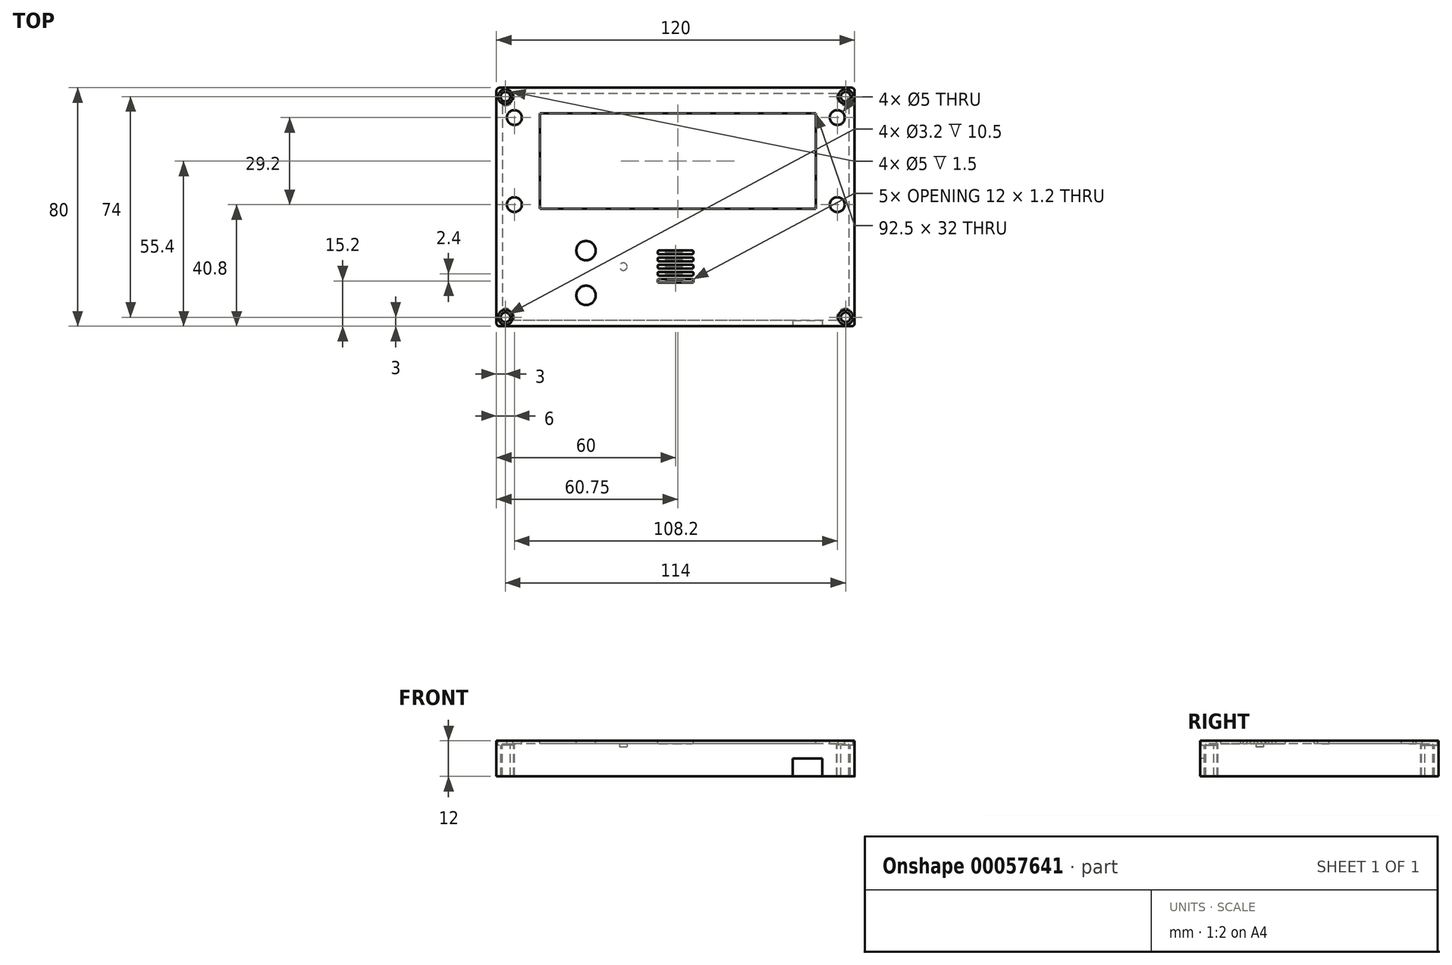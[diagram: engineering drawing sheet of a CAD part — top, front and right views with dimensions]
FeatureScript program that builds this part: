
annotation { "Feature Type Name" : "Feature", "Feature Type Description" : "" }
export const myFeature = defineFeature(function(context is Context, id is Id, definition is map)
    precondition{}
    {
        {
            var Q0;
            Q0=qCreatedBy(makeId("Top.planeOp"),FACE);
            var sketch = newSketch(context, id + "F0", { "sketchPlane" : qUnion([Q0])});
            skLineSegment(sketch, "E0.bottom", {"start": v(-60, 40) * mm, "end": v(60, 40) * mm});
            skLineSegment(sketch, "E0.top", {"start": v(-60, -40) * mm, "end": v(60, -40) * mm});
            skLineSegment(sketch, "E0.left", {"start": v(-60, 40) * mm, "end": v(-60, -40) * mm});
            skLineSegment(sketch, "E0.right", {"start": v(60, 40) * mm, "end": v(60, -40) * mm});
            skLineSegment(sketch, "E1.bottom", {"start": v(60, -40) * mm, "end": v(50, -40) * mm, "construction": true});
            skLineSegment(sketch, "E1.left", {"start": v(60, -40) * mm, "end": v(60, -25) * mm, "construction": true});
            skSolve(sketch);
        }
        {
            var Q0;
            Q0=makeQuery(id+"F0.imprint","IMPRINT",FACE,{"disambiguationData":[TD([[makeQuery(id+"F0.imprint","IMPRINT",EDGE,{"derivedFrom":sQuery(id+"F0.wireOp",EDGE,"E0.bottom")}),-1.0]])]});
            extrude(context, id + "F1", {"entities" : qUnion([Q0]), "depth" : 2 * mm});
        }
        {
            var Q0;
            Q0=makeQuery(id+"F1.opExtrude","CAP_FACE",FACE,{"disambiguationData":[OSD([sQuery(id+"F0.wireOp",EDGE,"E0.bottom"),sQuery(id+"F0.wireOp",EDGE,"E0.top"),sQuery(id+"F0.wireOp",EDGE,"E0.left"),sQuery(id+"F0.wireOp",EDGE,"E0.right")])],"isStart":false});
            var sketch = newSketch(context, id + "F2", { "sketchPlane" : qUnion([Q0])});
            skLineSegment(sketch, "E2.rect.bottom", {"start": v(58, 38) * mm, "end": v(-58, 38) * mm});
            skLineSegment(sketch, "E2.rect.top", {"start": v(58, -38) * mm, "end": v(-58, -38) * mm});
            skLineSegment(sketch, "E2.rect.left", {"start": v(58, 38) * mm, "end": v(58, -38) * mm});
            skLineSegment(sketch, "E2.rect.right", {"start": v(-58, 38) * mm, "end": v(-58, -38) * mm});
            skPoint(sketch, "E2.rect.middle", {"position": v(0, 0) * mm});
            skPoint(sketch, "E3", {"position": v(-57, 37) * mm});
            skCircle(sketch, "E4", {"center": v(-57, 37) * mm, "radius": 3 * mm});
            skPoint(sketch, "E5", {"position": v(-57, -37) * mm});
            skCircle(sketch, "E6", {"center": v(-57, -37) * mm, "radius": 3 * mm});
            skPoint(sketch, "E7", {"position": v(57, -37) * mm});
            skCircle(sketch, "E8", {"center": v(57, -37) * mm, "radius": 3 * mm});
            skPoint(sketch, "E9", {"position": v(57, 37) * mm});
            skCircle(sketch, "E10", {"center": v(57, 37) * mm, "radius": 3 * mm});
            skSolve(sketch);
        }
        {
            var Q0;
            {var subQ3=sQuery(id+"F2.wireOp",EDGE,"E2.rect.bottom");var subQ5=sQuery(id+"F2.wireOp",EDGE,"E2.rect.right");var subQ6=makeQuery(id+"F2.imprint","INTERSECT",VERTEX,{"derivedFrom":[subQ3,subQ5]});Q0=makeQuery(id+"F2.imprint","IMPRINT",FACE,{"disambiguationData":[TD([[makeQuery(id+"F2.imprint","IMPRINT",EDGE,{"disambiguationData":[TD([[subQ6,1.0]])],"derivedFrom":subQ3}),-1.0]])]});}
            var Q1;
            {var subQ0=sQuery(id+"F2.wireOp",EDGE,"E4");var subQ1=makeQuery(id+"F1.opExtrude","CAP_EDGE",EDGE,{"disambiguationData":[OSD([sQuery(id+"F0.wireOp",EDGE,"E0.bottom")])],"isStart":false});var subQ2=makeQuery(id+"F2.imprint","INTERSECT",VERTEX,{"derivedFrom":[subQ1,subQ0]});Q1=makeQuery(id+"F2.imprint","IMPRINT",FACE,{"disambiguationData":[TD([[makeQuery(id+"F2.imprint","IMPRINT",EDGE,{"disambiguationData":[TD([[subQ2,-1.0]])],"derivedFrom":subQ0}),-1.0]])]});}
            var Q2;
            {var subQ0=sQuery(id+"F2.wireOp",EDGE,"E2.rect.right");var subQ1=sQuery(id+"F2.wireOp",EDGE,"E2.rect.bottom");var subQ2=makeQuery(id+"F2.imprint","INTERSECT",VERTEX,{"derivedFrom":[subQ1,subQ0]});Q2=makeQuery(id+"F2.imprint","IMPRINT",FACE,{"disambiguationData":[TD([[makeQuery(id+"F2.imprint","IMPRINT",EDGE,{"disambiguationData":[TD([[subQ2,1.0]])],"derivedFrom":subQ1}),1.0]])]});}
            var Q3;
            {var subQ0=sQuery(id+"F2.wireOp",EDGE,"E4");var subQ1=sQuery(id+"F2.wireOp",EDGE,"E2.rect.right");var subQ2=makeQuery(id+"F2.imprint","INTERSECT",VERTEX,{"derivedFrom":[subQ1,subQ0]});Q3=makeQuery(id+"F2.imprint","IMPRINT",FACE,{"disambiguationData":[TD([[makeQuery(id+"F2.imprint","IMPRINT",EDGE,{"disambiguationData":[TD([[subQ2,-1.0]])],"derivedFrom":subQ1}),-1.0]])]});}
            var Q4;
            {var subQ0=sQuery(id+"F2.wireOp",EDGE,"E10");var subQ1=sQuery(id+"F2.wireOp",EDGE,"E2.rect.bottom");var subQ2=makeQuery(id+"F2.imprint","INTERSECT",VERTEX,{"derivedFrom":[subQ1,subQ0]});Q4=makeQuery(id+"F2.imprint","IMPRINT",FACE,{"disambiguationData":[TD([[makeQuery(id+"F2.imprint","IMPRINT",EDGE,{"disambiguationData":[TD([[subQ2,-1.0]])],"derivedFrom":subQ1}),-1.0]])]});}
            var Q5;
            {var subQ1=sQuery(id+"F2.wireOp",EDGE,"E2.rect.bottom");var subQ4=sQuery(id+"F2.wireOp",EDGE,"E2.rect.left");var subQ5=makeQuery(id+"F2.imprint","INTERSECT",VERTEX,{"derivedFrom":[subQ1,subQ4]});Q5=makeQuery(id+"F2.imprint","IMPRINT",FACE,{"disambiguationData":[TD([[makeQuery(id+"F2.imprint","IMPRINT",EDGE,{"disambiguationData":[TD([[subQ5,-1.0]])],"derivedFrom":subQ1}),-1.0]])]});}
            var Q6;
            {var subQ0=sQuery(id+"F2.wireOp",EDGE,"E2.rect.left");var subQ1=sQuery(id+"F2.wireOp",EDGE,"E2.rect.bottom");var subQ2=makeQuery(id+"F2.imprint","INTERSECT",VERTEX,{"derivedFrom":[subQ1,subQ0]});Q6=makeQuery(id+"F2.imprint","IMPRINT",FACE,{"disambiguationData":[TD([[makeQuery(id+"F2.imprint","IMPRINT",EDGE,{"disambiguationData":[TD([[subQ2,-1.0]])],"derivedFrom":subQ1}),1.0]])]});}
            var Q7;
            {var subQ0=sQuery(id+"F2.wireOp",EDGE,"E10");var subQ1=makeQuery(id+"F1.opExtrude","CAP_EDGE",EDGE,{"disambiguationData":[OSD([sQuery(id+"F0.wireOp",EDGE,"E0.bottom")])],"isStart":false});var subQ2=makeQuery(id+"F2.imprint","INTERSECT",VERTEX,{"derivedFrom":[subQ1,subQ0]});Q7=makeQuery(id+"F2.imprint","IMPRINT",FACE,{"disambiguationData":[TD([[makeQuery(id+"F2.imprint","IMPRINT",EDGE,{"disambiguationData":[TD([[subQ2,1.0]])],"derivedFrom":subQ0}),-1.0]])]});}
            var Q8;
            {var subQ0=sQuery(id+"F2.wireOp",EDGE,"E10");var subQ1=sQuery(id+"F2.wireOp",EDGE,"E2.rect.left");var subQ2=makeQuery(id+"F2.imprint","INTERSECT",VERTEX,{"derivedFrom":[subQ1,subQ0]});Q8=makeQuery(id+"F2.imprint","IMPRINT",FACE,{"disambiguationData":[TD([[makeQuery(id+"F2.imprint","IMPRINT",EDGE,{"disambiguationData":[TD([[subQ2,-1.0]])],"derivedFrom":subQ1}),1.0]])]});}
            var Q9;
            {var subQ0=sQuery(id+"F2.wireOp",EDGE,"E8");var subQ1=makeQuery(id+"F1.opExtrude","CAP_EDGE",EDGE,{"disambiguationData":[OSD([sQuery(id+"F0.wireOp",EDGE,"E0.right")])],"isStart":false});var subQ2=makeQuery(id+"F2.imprint","INTERSECT",VERTEX,{"derivedFrom":[subQ1,subQ0]});Q9=makeQuery(id+"F2.imprint","IMPRINT",FACE,{"disambiguationData":[TD([[makeQuery(id+"F2.imprint","IMPRINT",EDGE,{"disambiguationData":[TD([[subQ2,1.0]])],"derivedFrom":subQ0}),-1.0]])]});}
            var Q10;
            {var subQ1=sQuery(id+"F2.wireOp",EDGE,"E2.rect.top");var subQ4=sQuery(id+"F2.wireOp",EDGE,"E2.rect.left");var subQ5=makeQuery(id+"F2.imprint","INTERSECT",VERTEX,{"derivedFrom":[subQ1,subQ4]});Q10=makeQuery(id+"F2.imprint","IMPRINT",FACE,{"disambiguationData":[TD([[makeQuery(id+"F2.imprint","IMPRINT",EDGE,{"disambiguationData":[TD([[subQ5,-1.0]])],"derivedFrom":subQ1}),1.0]])]});}
            var Q11;
            {var subQ0=sQuery(id+"F2.wireOp",EDGE,"E2.rect.left");var subQ1=sQuery(id+"F2.wireOp",EDGE,"E2.rect.top");var subQ2=makeQuery(id+"F2.imprint","INTERSECT",VERTEX,{"derivedFrom":[subQ1,subQ0]});Q11=makeQuery(id+"F2.imprint","IMPRINT",FACE,{"disambiguationData":[TD([[makeQuery(id+"F2.imprint","IMPRINT",EDGE,{"disambiguationData":[TD([[subQ2,-1.0]])],"derivedFrom":subQ1}),-1.0]])]});}
            var Q12;
            {var subQ0=sQuery(id+"F2.wireOp",EDGE,"E8");var subQ1=sQuery(id+"F2.wireOp",EDGE,"E2.rect.top");var subQ2=makeQuery(id+"F2.imprint","INTERSECT",VERTEX,{"derivedFrom":[subQ1,subQ0]});Q12=makeQuery(id+"F2.imprint","IMPRINT",FACE,{"disambiguationData":[TD([[makeQuery(id+"F2.imprint","IMPRINT",EDGE,{"disambiguationData":[TD([[subQ2,-1.0]])],"derivedFrom":subQ1}),1.0]])]});}
            var Q13;
            {var subQ0=sQuery(id+"F2.wireOp",EDGE,"E6");var subQ1=makeQuery(id+"F1.opExtrude","CAP_EDGE",EDGE,{"disambiguationData":[OSD([sQuery(id+"F0.wireOp",EDGE,"E0.left")])],"isStart":false});var subQ2=makeQuery(id+"F2.imprint","INTERSECT",VERTEX,{"derivedFrom":[subQ1,subQ0]});Q13=makeQuery(id+"F2.imprint","IMPRINT",FACE,{"disambiguationData":[TD([[makeQuery(id+"F2.imprint","IMPRINT",EDGE,{"disambiguationData":[TD([[subQ2,-1.0]])],"derivedFrom":subQ0}),-1.0]])]});}
            var Q14;
            {var subQ3=sQuery(id+"F2.wireOp",EDGE,"E2.rect.right");var subQ5=sQuery(id+"F2.wireOp",EDGE,"E2.rect.top");var subQ6=makeQuery(id+"F2.imprint","INTERSECT",VERTEX,{"derivedFrom":[subQ5,subQ3]});Q14=makeQuery(id+"F2.imprint","IMPRINT",FACE,{"disambiguationData":[TD([[makeQuery(id+"F2.imprint","IMPRINT",EDGE,{"disambiguationData":[TD([[subQ6,1.0]])],"derivedFrom":subQ5}),1.0]])]});}
            var Q15;
            {var subQ0=sQuery(id+"F2.wireOp",EDGE,"E2.rect.right");var subQ1=sQuery(id+"F2.wireOp",EDGE,"E2.rect.top");var subQ2=makeQuery(id+"F2.imprint","INTERSECT",VERTEX,{"derivedFrom":[subQ1,subQ0]});Q15=makeQuery(id+"F2.imprint","IMPRINT",FACE,{"disambiguationData":[TD([[makeQuery(id+"F2.imprint","IMPRINT",EDGE,{"disambiguationData":[TD([[subQ2,1.0]])],"derivedFrom":subQ1}),-1.0]])]});}
            var Q16;
            {var subQ0=sQuery(id+"F2.wireOp",EDGE,"E6");var subQ1=sQuery(id+"F2.wireOp",EDGE,"E2.rect.top");var subQ2=makeQuery(id+"F2.imprint","INTERSECT",VERTEX,{"derivedFrom":[subQ1,subQ0]});Q16=makeQuery(id+"F2.imprint","IMPRINT",FACE,{"disambiguationData":[TD([[makeQuery(id+"F2.imprint","IMPRINT",EDGE,{"disambiguationData":[TD([[subQ2,-1.0]])],"derivedFrom":subQ1}),-1.0]])]});}
            var Q17;
            {var subQ0=sQuery(id+"F2.wireOp",EDGE,"77e153d8-aec5-4759-a28a-f8f5d5c03576");var subQ1=sQuery(id+"F2.wireOp",EDGE,"E2.rect.bottom");var subQ2=makeQuery(id+"F2.imprint","INTERSECT",VERTEX,{"derivedFrom":[subQ1,subQ0]});Q17=makeQuery(id+"F2.imprint","IMPRINT",FACE,{"disambiguationData":[TD([[makeQuery(id+"F2.imprint","IMPRINT",EDGE,{"disambiguationData":[TD([[subQ2,-1.0]])],"derivedFrom":subQ1}),1.0]])]});}
            var Q18;
            {var subQ0=sQuery(id+"F2.wireOp",EDGE,"bf45aabd-59fb-4a7d-bd56-748f739b5a62");var subQ1=sQuery(id+"F2.wireOp",EDGE,"E2.rect.top");var subQ2=makeQuery(id+"F2.imprint","INTERSECT",VERTEX,{"derivedFrom":[subQ1,subQ0]});Q18=makeQuery(id+"F2.imprint","IMPRINT",FACE,{"disambiguationData":[TD([[makeQuery(id+"F2.imprint","IMPRINT",EDGE,{"disambiguationData":[TD([[subQ2,-1.0]])],"derivedFrom":subQ1}),-1.0]])]});}
            var Q19;
            {var subQ0=sQuery(id+"F2.wireOp",EDGE,"E4");var subQ1=sQuery(id+"F2.wireOp",EDGE,"E2.rect.bottom");var subQ2=makeQuery(id+"F2.imprint","INTERSECT",VERTEX,{"derivedFrom":[subQ1,subQ0]});Q19=makeQuery(id+"F2.imprint","IMPRINT",FACE,{"disambiguationData":[TD([[makeQuery(id+"F2.imprint","IMPRINT",EDGE,{"disambiguationData":[TD([[subQ2,-1.0]])],"derivedFrom":subQ1}),1.0]])]});}
            extrude(context, id + "F3", {"entities" : qUnion([Q0, Q1, Q2, Q3, Q4, Q5, Q6, Q7, Q8, Q9, Q10, Q11, Q12, Q13, Q14, Q15, Q16, Q17, Q18, Q19]), "operationType" : NewBodyOperationType.ADD, "oppositeDirection" : true, "depth" : 12 * mm});
        }
        {
            var Q0;
            Q0=makeQuery(id+"F1.opExtrude","CAP_FACE",FACE,{"disambiguationData":[OSD([sQuery(id+"F0.wireOp",EDGE,"E0.bottom"),sQuery(id+"F0.wireOp",EDGE,"E0.top"),sQuery(id+"F0.wireOp",EDGE,"E0.left"),sQuery(id+"F0.wireOp",EDGE,"E0.right")])],"isStart":false});
            var sketch = newSketch(context, id + "F4", { "sketchPlane" : qUnion([Q0])});
            skPoint(sketch, "E11", {"position": v(-54, 30) * mm});
            skPoint(sketch, "E12", {"position": v(54.2, 30) * mm});
            skPoint(sketch, "E13", {"position": v(54.2, 0.8) * mm});
            skPoint(sketch, "E14", {"position": v(-54, 0.8) * mm});
            skLineSegment(sketch, "E15.rect.bottom", {"start": v(47, 31.4) * mm, "end": v(-45.5, 31.4) * mm});
            skLineSegment(sketch, "E15.rect.top", {"start": v(47, -0.6) * mm, "end": v(-45.5, -0.6) * mm});
            skLineSegment(sketch, "E15.rect.left", {"start": v(47, 31.4) * mm, "end": v(47, -0.6) * mm});
            skLineSegment(sketch, "E15.rect.right", {"start": v(-45.5, 31.4) * mm, "end": v(-45.5, -0.6) * mm});
            skPoint(sketch, "E15.rect.middle", {"position": v(0, 15.4) * mm});
            skSolve(sketch);
        }
        {
            var Q0;
            Q0=sQuery(id+"F4.wireOp",VERTEX,"E11");
            var Q1;
            Q1=sQuery(id+"F4.wireOp",VERTEX,"E14");
            var Q2;
            Q2=sQuery(id+"F4.wireOp",VERTEX,"E13");
            var Q3;
            Q3=sQuery(id+"F4.wireOp",VERTEX,"E12");
            var Q4;
            Q4=makeQuery(id+"F1.opExtrude","SWEPT_BODY",BODY,{"disambiguationData":[OSD([sQuery(id+"F0.wireOp",EDGE,"E0.bottom"),sQuery(id+"F0.wireOp",EDGE,"E0.top"),sQuery(id+"F0.wireOp",EDGE,"E0.left"),sQuery(id+"F0.wireOp",EDGE,"E0.right")])]});
            hole(context, id + "F5", {"style" : HoleStyle.C_BORE, "holeDiameter" : 3 * mm, "cBoreDiameter" : 5 * mm, "cBoreDepth" : 1 * mm, "endStyle" : HoleEndStyle.THROUGH, "locations" : qUnion([Q0, Q1, Q2, Q3]), "scope" : qUnion([Q4])});
        }
        {
            var Q0;
            Q0 = qSketchRegion(id + "F4", true);
            extrude(context, id + "F6", {"entities" : qUnion([Q0]), "operationType" : NewBodyOperationType.REMOVE, "oppositeDirection" : true, "depth" : 3 * mm});
        }
        {
            var Q0;
            {var subQ0=sQuery(id+"F0.wireOp",EDGE,"E0.top");Q0=makeQuery(id+"F3.boolean.opBoolean","MERGE",FACE,{"derivedFrom":[makeQuery(id+"F1.opExtrude","SWEPT_FACE",FACE,{"disambiguationData":[OSD([subQ0])]}),makeQuery(id+"F3.opExtrude","SWEPT_FACE",FACE,{"disambiguationData":[OSD([subQ0])]})]});}
            var sketch = newSketch(context, id + "F7", { "sketchPlane" : qUnion([Q0])});
            skLineSegment(sketch, "E16.rect.bottom", {"start": v(49.2, -4) * mm, "end": v(39.2, -4) * mm});
            skLineSegment(sketch, "E16.rect.top", {"start": v(49.2, -16) * mm, "end": v(39.2, -16) * mm});
            skLineSegment(sketch, "E16.rect.left", {"start": v(49.2, -4) * mm, "end": v(49.2, -16) * mm});
            skLineSegment(sketch, "E16.rect.right", {"start": v(39.2, -4) * mm, "end": v(39.2, -16) * mm});
            skPoint(sketch, "E16.rect.middle", {"position": v(44.2, -10) * mm});
            skSolve(sketch);
        }
        {
            var Q0;
            {var subQ0=sQuery(id+"F7.wireOp",EDGE,"E16.rect.bottom");Q0=makeQuery(id+"F7.imprint","IMPRINT",FACE,{"disambiguationData":[TD([[makeQuery(id+"F7.imprint","IMPRINT",EDGE,{"derivedFrom":subQ0}),1.0]])]});}
            extrude(context, id + "F8", {"entities" : qUnion([Q0]), "operationType" : NewBodyOperationType.REMOVE, "oppositeDirection" : true, "depth" : 3 * mm});
        }
        {
            var Q0;
            {var subQ0=sQuery(id+"F0.wireOp",EDGE,"E0.right");var subQ1=sQuery(id+"F0.wireOp",EDGE,"E0.top");Q0=makeQuery(id+"F3.boolean.opBoolean","MERGE",EDGE,{"derivedFrom":[makeQuery(id+"F1.opExtrude","SWEPT_EDGE",EDGE,{"disambiguationData":[OSD([subQ1,subQ0])]}),makeQuery(id+"F3.opExtrude","SWEPT_EDGE",EDGE,{"disambiguationData":[OSD([subQ1,subQ0])]})]});}
            var Q1;
            {var subQ0=sQuery(id+"F0.wireOp",EDGE,"E0.right");var subQ1=sQuery(id+"F0.wireOp",EDGE,"E0.bottom");Q1=makeQuery(id+"F3.boolean.opBoolean","MERGE",EDGE,{"derivedFrom":[makeQuery(id+"F1.opExtrude","SWEPT_EDGE",EDGE,{"disambiguationData":[OSD([subQ1,subQ0])]}),makeQuery(id+"F3.opExtrude","SWEPT_EDGE",EDGE,{"disambiguationData":[OSD([subQ1,subQ0])]})]});}
            var Q2;
            {var subQ0=sQuery(id+"F0.wireOp",EDGE,"E0.left");var subQ1=sQuery(id+"F0.wireOp",EDGE,"E0.top");Q2=makeQuery(id+"F3.boolean.opBoolean","MERGE",EDGE,{"derivedFrom":[makeQuery(id+"F1.opExtrude","SWEPT_EDGE",EDGE,{"disambiguationData":[OSD([subQ1,subQ0])]}),makeQuery(id+"F3.opExtrude","SWEPT_EDGE",EDGE,{"disambiguationData":[OSD([subQ1,subQ0])]})]});}
            var Q3;
            {var subQ0=sQuery(id+"F0.wireOp",EDGE,"E0.left");var subQ1=sQuery(id+"F0.wireOp",EDGE,"E0.bottom");Q3=makeQuery(id+"F3.boolean.opBoolean","MERGE",EDGE,{"derivedFrom":[makeQuery(id+"F1.opExtrude","SWEPT_EDGE",EDGE,{"disambiguationData":[OSD([subQ1,subQ0])]}),makeQuery(id+"F3.opExtrude","SWEPT_EDGE",EDGE,{"disambiguationData":[OSD([subQ1,subQ0])]})]});}
            fillet(context, id + "F9", {"entities" : qUnion([Q0, Q1, Q2, Q3]), "radius" : 1 * mm, "tangentPropagation" : true, "allowEdgeOverflow" : false});
        }
        {
            var Q0;
            Q0=makeQuery(id+"F1.opExtrude","CAP_FACE",FACE,{"disambiguationData":[OSD([sQuery(id+"F0.wireOp",EDGE,"E0.bottom"),sQuery(id+"F0.wireOp",EDGE,"E0.top"),sQuery(id+"F0.wireOp",EDGE,"E0.left"),sQuery(id+"F0.wireOp",EDGE,"E0.right")])],"isStart":false});
            var sketch = newSketch(context, id + "F10", { "sketchPlane" : qUnion([Q0])});
            skPoint(sketch, "E17", {"position": v(-30, -14.64) * mm});
            skCircle(sketch, "E18", {"center": v(-30, -14.64) * mm, "radius": 3.25 * mm});
            skPoint(sketch, "E19", {"position": v(-30, -29.64) * mm});
            skCircle(sketch, "E20", {"center": v(-30, -29.64) * mm, "radius": 3.25 * mm});
            skLineSegment(sketch, "E21.rect.bottom", {"start": v(5.6, -15.8) * mm, "end": v(-5.6, -15.8) * mm});
            skLineSegment(sketch, "E21.rect.top", {"start": v(5.6, -14.6) * mm, "end": v(-5.6, -14.6) * mm});
            skLineSegment(sketch, "E21.rect.left", {"start": v(6, -15.4) * mm, "end": v(6, -15) * mm});
            skLineSegment(sketch, "E21.rect.right", {"start": v(-6, -15.4) * mm, "end": v(-6, -15) * mm});
            skPoint(sketch, "E21.rect.middle", {"position": v(0, -15.2) * mm});
            skPoint(sketch, "E22.visualSharp", {"position": v(-6, -14.6) * mm});
            skArc(sketch, "E22.filletArc", {"start": v(-5.6, -14.6) * mm, "mid": v(-5.88, -14.72) * mm, "end": v(-6, -15) * mm});
            skPoint(sketch, "E23.visualSharp", {"position": v(-6, -15.8) * mm});
            skArc(sketch, "E23.filletArc", {"start": v(-6, -15.4) * mm, "mid": v(-5.88, -15.68) * mm, "end": v(-5.6, -15.8) * mm});
            skPoint(sketch, "E24.visualSharp", {"position": v(6, -14.6) * mm});
            skArc(sketch, "E24.filletArc", {"start": v(6, -15) * mm, "mid": v(5.88, -14.72) * mm, "end": v(5.6, -14.6) * mm});
            skPoint(sketch, "E25.visualSharp", {"position": v(6, -15.8) * mm});
            skArc(sketch, "E25.filletArc", {"start": v(5.6, -15.8) * mm, "mid": v(5.88, -15.68) * mm, "end": v(6, -15.4) * mm});
            skPoint(sketch, "E26.0.1.0", {"position": v(0, -17.6) * mm});
            skLineSegment(sketch, "E26.0.1.1", {"start": v(5.6, -17) * mm, "end": v(-5.6, -17) * mm});
            skLineSegment(sketch, "E26.0.1.2", {"start": v(5.6, -18.2) * mm, "end": v(-5.6, -18.2) * mm});
            skPoint(sketch, "E26.0.1.3", {"position": v(-6, -18.2) * mm});
            skPoint(sketch, "E26.0.1.4", {"position": v(-6, -17) * mm});
            skPoint(sketch, "E26.0.1.5", {"position": v(6, -17) * mm});
            skPoint(sketch, "E26.0.1.6", {"position": v(6, -18.2) * mm});
            skArc(sketch, "E26.0.1.7", {"start": v(5.6, -18.2) * mm, "mid": v(5.88, -18.08) * mm, "end": v(6, -17.8) * mm});
            skLineSegment(sketch, "E26.0.1.8", {"start": v(6, -17.8) * mm, "end": v(6, -17.4) * mm});
            skLineSegment(sketch, "E26.0.1.9", {"start": v(-6, -17.8) * mm, "end": v(-6, -17.4) * mm});
            skArc(sketch, "E26.0.1.10", {"start": v(-5.6, -17) * mm, "mid": v(-5.88, -17.12) * mm, "end": v(-6, -17.4) * mm});
            skArc(sketch, "E26.0.1.11", {"start": v(6, -17.4) * mm, "mid": v(5.88, -17.12) * mm, "end": v(5.6, -17) * mm});
            skArc(sketch, "E26.0.1.12", {"start": v(-6, -17.8) * mm, "mid": v(-5.88, -18.08) * mm, "end": v(-5.6, -18.2) * mm});
            skPoint(sketch, "E26.0.2.0", {"position": v(0, -20) * mm});
            skLineSegment(sketch, "E26.0.2.1", {"start": v(5.6, -19.4) * mm, "end": v(-5.6, -19.4) * mm});
            skLineSegment(sketch, "E26.0.2.2", {"start": v(5.6, -20.6) * mm, "end": v(-5.6, -20.6) * mm});
            skPoint(sketch, "E26.0.2.3", {"position": v(-6, -20.6) * mm});
            skPoint(sketch, "E26.0.2.4", {"position": v(-6, -19.4) * mm});
            skPoint(sketch, "E26.0.2.5", {"position": v(6, -19.4) * mm});
            skPoint(sketch, "E26.0.2.6", {"position": v(6, -20.6) * mm});
            skArc(sketch, "E26.0.2.7", {"start": v(5.6, -20.6) * mm, "mid": v(5.88, -20.48) * mm, "end": v(6, -20.2) * mm});
            skLineSegment(sketch, "E26.0.2.8", {"start": v(6, -20.2) * mm, "end": v(6, -19.8) * mm});
            skLineSegment(sketch, "E26.0.2.9", {"start": v(-6, -20.2) * mm, "end": v(-6, -19.8) * mm});
            skArc(sketch, "E26.0.2.10", {"start": v(-5.6, -19.4) * mm, "mid": v(-5.88, -19.52) * mm, "end": v(-6, -19.8) * mm});
            skArc(sketch, "E26.0.2.11", {"start": v(6, -19.8) * mm, "mid": v(5.88, -19.52) * mm, "end": v(5.6, -19.4) * mm});
            skArc(sketch, "E26.0.2.12", {"start": v(-6, -20.2) * mm, "mid": v(-5.88, -20.48) * mm, "end": v(-5.6, -20.6) * mm});
            skPoint(sketch, "E26.0.3.0", {"position": v(0, -22.4) * mm});
            skLineSegment(sketch, "E26.0.3.1", {"start": v(5.6, -21.8) * mm, "end": v(-5.6, -21.8) * mm});
            skLineSegment(sketch, "E26.0.3.2", {"start": v(5.6, -23) * mm, "end": v(-5.6, -23) * mm});
            skPoint(sketch, "E26.0.3.3", {"position": v(-6, -23) * mm});
            skPoint(sketch, "E26.0.3.4", {"position": v(-6, -21.8) * mm});
            skPoint(sketch, "E26.0.3.5", {"position": v(6, -21.8) * mm});
            skPoint(sketch, "E26.0.3.6", {"position": v(6, -23) * mm});
            skArc(sketch, "E26.0.3.7", {"start": v(5.6, -23) * mm, "mid": v(5.88, -22.88) * mm, "end": v(6, -22.6) * mm});
            skLineSegment(sketch, "E26.0.3.8", {"start": v(6, -22.6) * mm, "end": v(6, -22.2) * mm});
            skLineSegment(sketch, "E26.0.3.9", {"start": v(-6, -22.6) * mm, "end": v(-6, -22.2) * mm});
            skArc(sketch, "E26.0.3.10", {"start": v(-5.6, -21.8) * mm, "mid": v(-5.88, -21.92) * mm, "end": v(-6, -22.2) * mm});
            skArc(sketch, "E26.0.3.11", {"start": v(6, -22.2) * mm, "mid": v(5.88, -21.92) * mm, "end": v(5.6, -21.8) * mm});
            skArc(sketch, "E26.0.3.12", {"start": v(-6, -22.6) * mm, "mid": v(-5.88, -22.88) * mm, "end": v(-5.6, -23) * mm});
            skPoint(sketch, "E26.0.4.0", {"position": v(0, -24.8) * mm});
            skLineSegment(sketch, "E26.0.4.1", {"start": v(5.6, -24.2) * mm, "end": v(-5.6, -24.2) * mm});
            skLineSegment(sketch, "E26.0.4.2", {"start": v(5.6, -25.4) * mm, "end": v(-5.6, -25.4) * mm});
            skPoint(sketch, "E26.0.4.3", {"position": v(-6, -25.4) * mm});
            skPoint(sketch, "E26.0.4.4", {"position": v(-6, -24.2) * mm});
            skPoint(sketch, "E26.0.4.5", {"position": v(6, -24.2) * mm});
            skPoint(sketch, "E26.0.4.6", {"position": v(6, -25.4) * mm});
            skArc(sketch, "E26.0.4.7", {"start": v(5.6, -25.4) * mm, "mid": v(5.88, -25.28) * mm, "end": v(6, -25) * mm});
            skLineSegment(sketch, "E26.0.4.8", {"start": v(6, -25) * mm, "end": v(6, -24.6) * mm});
            skLineSegment(sketch, "E26.0.4.9", {"start": v(-6, -25) * mm, "end": v(-6, -24.6) * mm});
            skArc(sketch, "E26.0.4.10", {"start": v(-5.6, -24.2) * mm, "mid": v(-5.88, -24.32) * mm, "end": v(-6, -24.6) * mm});
            skArc(sketch, "E26.0.4.11", {"start": v(6, -24.6) * mm, "mid": v(5.88, -24.32) * mm, "end": v(5.6, -24.2) * mm});
            skArc(sketch, "E26.0.4.12", {"start": v(-6, -25) * mm, "mid": v(-5.88, -25.28) * mm, "end": v(-5.6, -25.4) * mm});
            skLineSegment(sketch, "E26.direction1", {"start": v(0, -15.2) * mm, "end": v(25, -15.2) * mm, "construction": true});
            skLineSegment(sketch, "E26.direction2", {"start": v(0, -15.2) * mm, "end": v(0, -17.6) * mm, "construction": true});
            skSolve(sketch);
        }
        {
            var Q0;
            Q0=makeQuery(id+"F10.imprint","IMPRINT",FACE,{"disambiguationData":[TD([[makeQuery(id+"F10.imprint","IMPRINT",EDGE,{"derivedFrom":sQuery(id+"F10.wireOp",EDGE,"E18")}),1.0]])]});
            var Q1;
            Q1=makeQuery(id+"F10.imprint","IMPRINT",FACE,{"disambiguationData":[TD([[makeQuery(id+"F10.imprint","IMPRINT",EDGE,{"derivedFrom":sQuery(id+"F10.wireOp",EDGE,"E20")}),1.0]])]});
            var Q2;
            Q2=makeQuery(id+"F10.imprint","IMPRINT",FACE,{"disambiguationData":[TD([[makeQuery(id+"F10.imprint","IMPRINT",EDGE,{"derivedFrom":sQuery(id+"F10.wireOp",EDGE,"E21.rect.bottom")}),-1.0]])]});
            var Q3;
            Q3=makeQuery(id+"F10.imprint","IMPRINT",FACE,{"disambiguationData":[TD([[makeQuery(id+"F10.imprint","IMPRINT",EDGE,{"derivedFrom":sQuery(id+"F10.wireOp",EDGE,"E26.0.1.1")}),1.0]])]});
            var Q4;
            Q4=makeQuery(id+"F10.imprint","IMPRINT",FACE,{"disambiguationData":[TD([[makeQuery(id+"F10.imprint","IMPRINT",EDGE,{"derivedFrom":sQuery(id+"F10.wireOp",EDGE,"E26.0.2.1")}),1.0]])]});
            var Q5;
            Q5=makeQuery(id+"F10.imprint","IMPRINT",FACE,{"disambiguationData":[TD([[makeQuery(id+"F10.imprint","IMPRINT",EDGE,{"derivedFrom":sQuery(id+"F10.wireOp",EDGE,"E26.0.3.1")}),1.0]])]});
            var Q6;
            Q6=makeQuery(id+"F10.imprint","IMPRINT",FACE,{"disambiguationData":[TD([[makeQuery(id+"F10.imprint","IMPRINT",EDGE,{"derivedFrom":sQuery(id+"F10.wireOp",EDGE,"E26.0.4.1")}),1.0]])]});
            extrude(context, id + "F11", {"entities" : qUnion([Q0, Q1, Q2, Q3, Q4, Q5, Q6]), "operationType" : NewBodyOperationType.REMOVE, "endBound" : BoundingType.UP_TO_NEXT, "oppositeDirection" : true, "depth" : 3 * mm});
        }
        {
            var Q0;
            Q0=makeQuery(id+"F1.opExtrude","CAP_FACE",FACE,{"disambiguationData":[OSD([sQuery(id+"F0.wireOp",EDGE,"E0.bottom"),sQuery(id+"F0.wireOp",EDGE,"E0.top"),sQuery(id+"F0.wireOp",EDGE,"E0.left"),sQuery(id+"F0.wireOp",EDGE,"E0.right")])],"isStart":true});
            var sketch = newSketch(context, id + "F12", { "sketchPlane" : qUnion([Q0])});
            skPoint(sketch, "E27", {"position": v(17.5, 20) * mm});
            skPoint(sketch, "E27.positionSnap0", {"position": v(6, 20) * mm});
            skCircle(sketch, "E28", {"center": v(17.5, 20) * mm, "radius": 1.25 * mm});
            skCircle(sketch, "E29.MirrorC", {"center": v(-17.5, 20) * mm, "radius": 1.25 * mm});
            skSolve(sketch);
        }
        {
            var Q0;
            Q0=makeQuery(id+"F12.imprint","IMPRINT",FACE,{"disambiguationData":[TD([[makeQuery(id+"F12.imprint","IMPRINT",EDGE,{"derivedFrom":sQuery(id+"F12.wireOp",EDGE,"E28")}),1.0]])]});
            var Q1;
            Q1=makeQuery(id+"F12.imprint","IMPRINT",FACE,{"disambiguationData":[TD([[makeQuery(id+"F12.imprint","IMPRINT",EDGE,{"derivedFrom":sQuery(id+"F12.wireOp",EDGE,"E29.MirrorC")}),-1.0]])]});
            extrude(context, id + "F13", {"entities" : qUnion([Q0, Q1]), "operationType" : NewBodyOperationType.REMOVE, "oppositeDirection" : true, "depth" : 1 * mm});
        }
        {
            var Q0;
            Q0=makeQuery(id+"F1.opExtrude","CAP_FACE",FACE,{"disambiguationData":[OSD([sQuery(id+"F0.wireOp",EDGE,"E0.bottom"),sQuery(id+"F0.wireOp",EDGE,"E0.top"),sQuery(id+"F0.wireOp",EDGE,"E0.left"),sQuery(id+"F0.wireOp",EDGE,"E0.right")])],"isStart":false});
            var sketch = newSketch(context, id + "F14", { "sketchPlane" : qUnion([Q0])});
            skPoint(sketch, "E30", {"position": v(-57, 37) * mm});
            skPoint(sketch, "E31.MirrorP", {"position": v(57, 37) * mm});
            skPoint(sketch, "E32.MirrorP", {"position": v(-57, -37) * mm});
            skPoint(sketch, "E33.MirrorP", {"position": v(57, -37) * mm});
            skSolve(sketch);
        }
        {
            var Q0;
            Q0=sQuery(id+"F14.wireOp",VERTEX,"E30");
            var Q1;
            Q1=sQuery(id+"F14.wireOp",VERTEX,"E31.MirrorP");
            var Q2;
            Q2=sQuery(id+"F14.wireOp",VERTEX,"E33.MirrorP");
            var Q3;
            Q3=sQuery(id+"F14.wireOp",VERTEX,"E32.MirrorP");
            var Q4;
            Q4=makeQuery(id+"F1.opExtrude","SWEPT_BODY",BODY,{"disambiguationData":[OSD([sQuery(id+"F0.wireOp",EDGE,"E0.bottom"),sQuery(id+"F0.wireOp",EDGE,"E0.top"),sQuery(id+"F0.wireOp",EDGE,"E0.left"),sQuery(id+"F0.wireOp",EDGE,"E0.right")])]});
            hole(context, id + "F15", {"style" : HoleStyle.C_BORE, "holeDiameter" : 3.2 * mm, "cBoreDiameter" : 5 * mm, "cBoreDepth" : 1.5 * mm, "endStyle" : HoleEndStyle.THROUGH, "locations" : qUnion([Q0, Q1, Q2, Q3]), "scope" : qUnion([Q4])});
        }
    });
